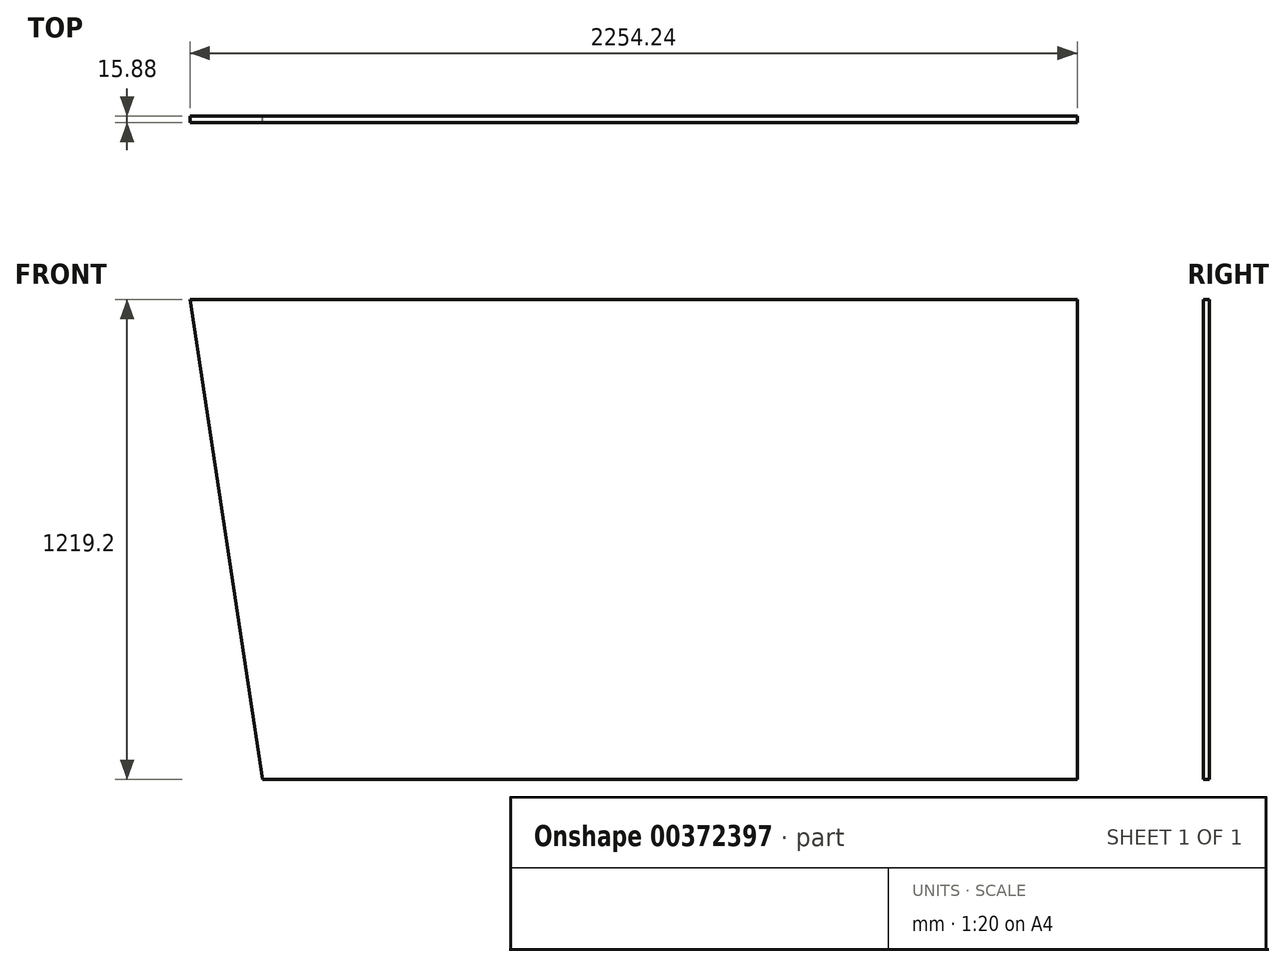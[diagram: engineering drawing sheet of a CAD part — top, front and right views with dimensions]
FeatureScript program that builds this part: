
annotation { "Feature Type Name" : "Feature", "Feature Type Description" : "" }
export const myFeature = defineFeature(function(context is Context, id is Id, definition is map)
    precondition{}
    {
        {
            var Q0;
            Q0=qCreatedBy(makeId("Front.planeOp"),FACE);
            var sketch = newSketch(context, id + "F0", { "sketchPlane" : qUnion([Q0])});
            skLineSegment(sketch, "E0.bottom", {"start": v(1127.13, -609.6) * mm, "end": v(-942.98, -609.6) * mm});
            skLineSegment(sketch, "E0.top", {"start": v(1127.13, 609.6) * mm, "end": v(-1127.13, 609.6) * mm});
            skLineSegment(sketch, "E0.left", {"start": v(1127.13, -609.6) * mm, "end": v(1127.13, 609.6) * mm});
            skPoint(sketch, "E0.middle", {"position": v(0, 0) * mm});
            skLineSegment(sketch, "E1", {"start": v(-1127.13, 609.6) * mm, "end": v(-942.98, -609.6) * mm});
            skPoint(sketch, "E2.orphan", {"position": v(-1127.13, -609.6) * mm});
            skSolve(sketch);
        }
        {
            var Q0;
            Q0=qSketchRegion(id+"F0",true);
            extrude(context, id + "F1", {"entities" : qUnion([Q0]), "depth" : 15.88 * mm});
        }
    });
